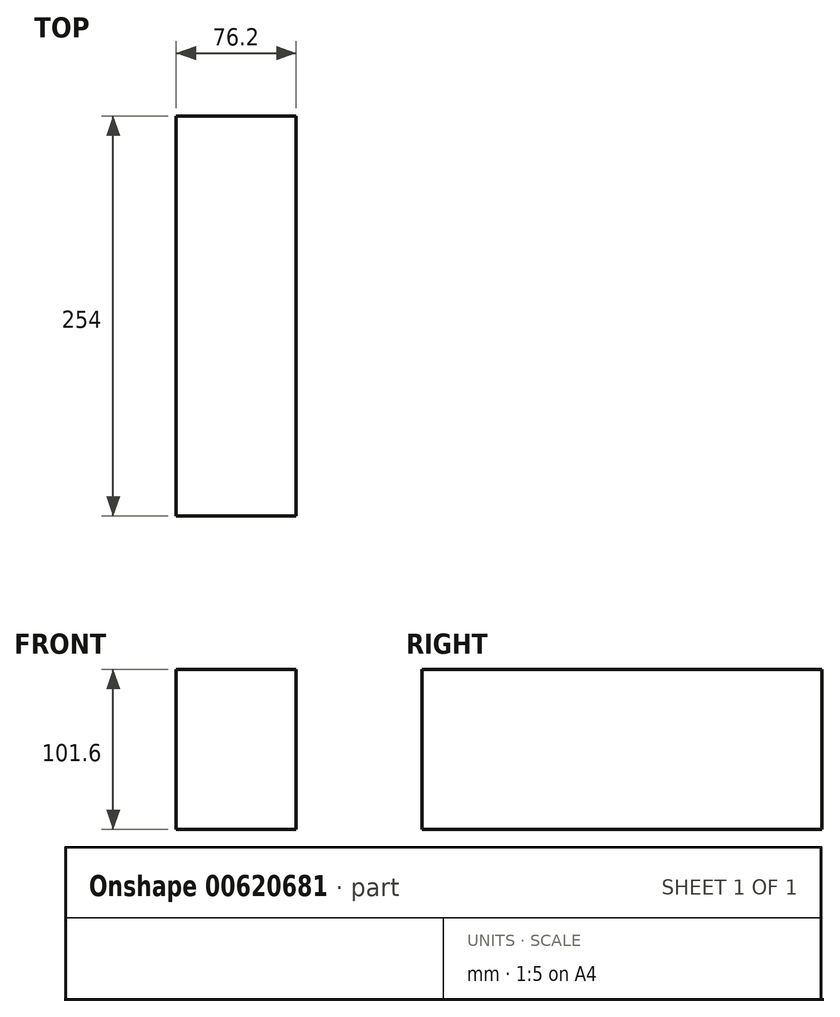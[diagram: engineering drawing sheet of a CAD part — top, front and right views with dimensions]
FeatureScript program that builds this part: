
annotation { "Feature Type Name" : "Feature", "Feature Type Description" : "" }
export const myFeature = defineFeature(function(context is Context, id is Id, definition is map)
    precondition{}
    {
        {
            var Q0;
            Q0=qCreatedBy(makeId("Top.planeOp"),FACE);
            var sketch = newSketch(context, id + "F0", { "sketchPlane" : qUnion([Q0])});
            skLineSegment(sketch, "E0.bottom", {"start": v(0, 0) * mm, "end": v(76.2, 0) * mm});
            skLineSegment(sketch, "E0.top", {"start": v(0, 254) * mm, "end": v(76.2, 254) * mm});
            skLineSegment(sketch, "E0.left", {"start": v(0, 0) * mm, "end": v(0, 254) * mm});
            skLineSegment(sketch, "E0.right", {"start": v(76.2, 0) * mm, "end": v(76.2, 254) * mm});
            skSolve(sketch);
        }
        {
            var Q0;
            Q0=makeQuery(id+"F0.imprint","IMPRINT",FACE,{"disambiguationData":[TD([[makeQuery(id+"F0.imprint","IMPRINT",EDGE,{"derivedFrom":sQuery(id+"F0.wireOp",EDGE,"E0.bottom")}),1.0]])]});
            extrude(context, id + "F1", {"entities" : qUnion([Q0]), "depth" : 101.6 * mm, "offsetDistance" : 25.4 * mm});
        }
    });
